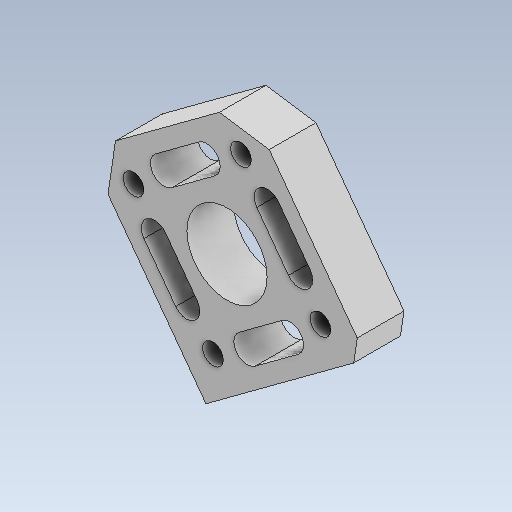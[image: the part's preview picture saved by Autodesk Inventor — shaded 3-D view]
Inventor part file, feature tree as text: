
AUTODESK INVENTOR PART (.ipt)
format: ipt  version: 2020 (Build 240168000, 168)  size: 219,136 bytes
history: native  units: mm
features: thicken_offset x8, other x3, sketch x2, extrude x2, plane x1, pattern_circular x1, chamfer x1, reference x1, projected_geometry x1
ambient origin geometry x8: Origin, YZ Plane, XZ Plane, XY Plane, X Axis, Y Axis, Z Axis, Center Point
bodies: Solid1 (feature_tree)
feature tree (20):
  sketch  "Sketch1"  dims[d0=12.0mm d1=30.0mm]
  plane  "Work Plane1"
  extrude  "Extrusion1"  Depth=30.0mm
  extrude  "Extrusion2"  Depth=10.0mm TaperAngle=0.0deg
  pattern_circular  "Circular Pattern1"  [2 undecoded]
  chamfer  "Chamfer1"  Distance=4.0mm
  thicken_offset  "Thicken1"
  thicken_offset  "Thicken2"
  thicken_offset  "Thicken3"
  thicken_offset  "Thicken4"
  thicken_offset  "Thicken5"
  thicken_offset  "Thicken6"
  thicken_offset  "Thicken7"
  thicken_offset  "Thicken8"
  reference  "Reference1"
  sketch  "Sketch2"  dims[d2=31.0mm d3=10.0mm d4=0.0mm d5=0.5mm d6=4.0mm d7=4.0mm d8=10.0mm d9=0.0mm d10=40.0mm d11=360.0deg d13=3.0mm d14=2.0mm d15=45.0deg d16=0.5mm d17=0.5mm d18=0.5mm d19=0.5mm d20=0.5mm d21=0.5mm d22=0.5mm d23=0.5mm d24=0.5mm d25=0.5mm d26=0.5mm d27=0.5mm d28=2.0mm d29=0.5mm d30=2.0mm d31=0.5mm]
  projected_geometry  "Projected Loop1"
  parser-record x1  (decoder bookkeeping rows leaked as tree rows — omitted from the tree; the rows remain in map.json)
  other  "reducer_1.iam"
  other  "motor_holder_5:1"
note: 2 required parameter values undecoded (feature->parameter linkage not recoverable at this tier; creation-order binding heuristic only, values carry confidence <= 0.55)
note: 1 file-system path scrubbed to <path> (originals preserved in map.json)
